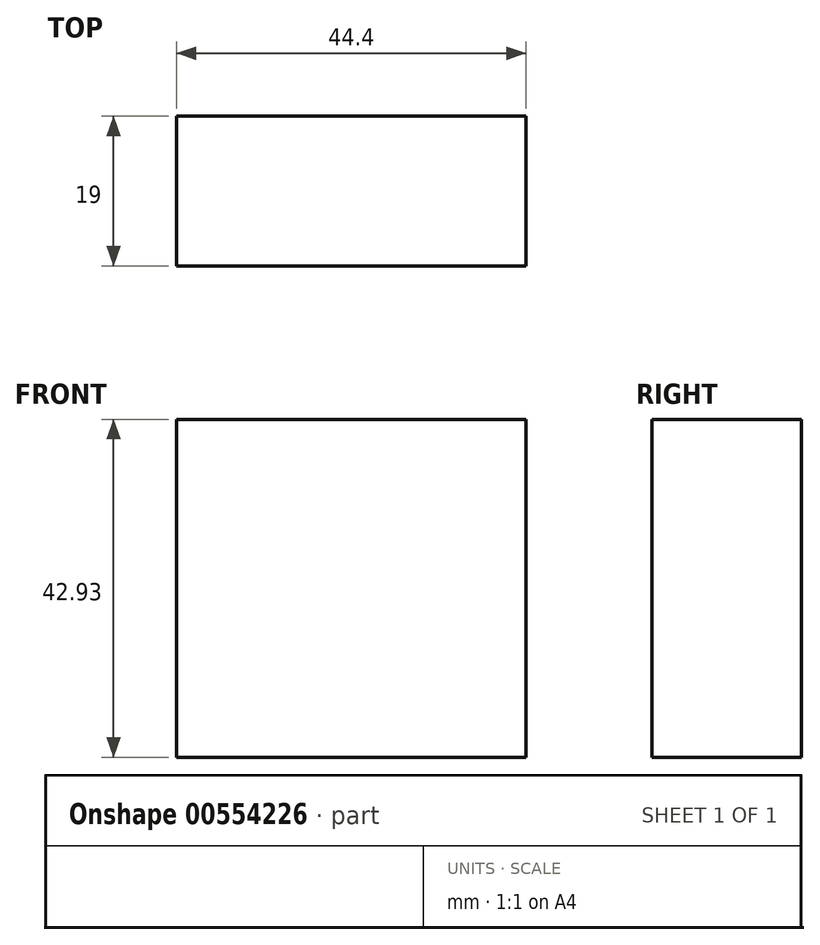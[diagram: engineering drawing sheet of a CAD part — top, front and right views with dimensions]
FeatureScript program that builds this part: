
annotation { "Feature Type Name" : "Feature", "Feature Type Description" : "" }
export const myFeature = defineFeature(function(context is Context, id is Id, definition is map)
    precondition{}
    {
        {
            var Q0;
            Q0=qCreatedBy(makeId("Top.planeOp"),FACE);
            var sketch = newSketch(context, id + "F0", { "sketchPlane" : qUnion([Q0])});
            skLineSegment(sketch, "E0.bottom", {"start": v(0, 0) * mm, "end": v(44.4, 0) * mm});
            skLineSegment(sketch, "E0.top", {"start": v(0, 19) * mm, "end": v(44.4, 19) * mm});
            skLineSegment(sketch, "E0.left", {"start": v(0, 0) * mm, "end": v(0, 19) * mm});
            skLineSegment(sketch, "E0.right", {"start": v(44.4, 0) * mm, "end": v(44.4, 19) * mm});
            skSolve(sketch);
        }
        {
            var Q0;
            Q0 = qSketchRegion(id + "F0", true);
            extrude(context, id + "F1", {"entities" : qUnion([Q0]), "depth" : 42.93 * mm, "offsetDistance" : 25.4 * mm});
        }
    });
